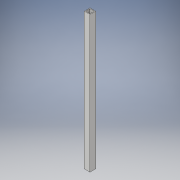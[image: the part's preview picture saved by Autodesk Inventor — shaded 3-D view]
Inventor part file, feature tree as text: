
AUTODESK INVENTOR PART (.ipt)
format: ipt  version: 2018 (Build 220112000, 112)  size: 97,792 bytes
history: native  units: in
note: dims shown in document units (in); Inventor stores cm internally (conversion verified against a paired STEP export)
features: extrude x1, sketch x1
ambient origin geometry x8: Origin, YZ Plane, XZ Plane, XY Plane, X Axis, Y Axis, Z Axis, Center Point
bodies: Solid1 (feature_tree)
feature tree (2):
  extrude  "Extrusion1"  Depth=1.0in
  sketch  "Sketch1"  dims[d0=1.0in d1=1.0in d2=0.125in d3=24.0in d4=0.0in]
